# Revit family: 54212209(2024)
name_source: partatom
category: Plumbing Fixtures
units: mm (PartAtom-declared; Revit-internal decimal feet)

## family parameters
Always vertical = Yes
Cut with Voids When Loaded = No
OmniClass Number = 23.45.55.00
OmniClass Title = Sanitary Faucets, Wastes
Part Type = Normal
Room Calculation Point = No
Round Connector Dimension = Use Diameter
Shared = No
Work Plane-Based = No

## types (3) — shared parameters
2D/3D/BIM Files URL = http://static.hansa.com
3D View = https://static.hansa.com
Advanced Features = Inner body made of DZR brass
Aerator = Standard aerator
AssetType = Fixed
Automatic Flush Frequency = 30 s (1-1800 s)
Automatic Flush Period = 30 s (1-1800 s)
Backflow Prevention EN1717 = EB
Bluetooth = 5.x (D060576)
BodyMaterial = Brass
Brand = HANSA
Catalog Drawing URL = http://static.hansa.com
Connection = Flexible inlet pipes
Connection Size = G3/8
Dimension Drawing URL = http://static.hansa.com
DurationUnit = Year
EMC Directive = Radio Equipment Directive 2014/53/EU , 
Low Voltage Directive 2014/35/EU , 
EMC Directive 2014/30/EU , 
RoHS Directive 2011/65/EU
EN Standard = ETSI EN 301 489-1 V1.9.2 , 
ETSI EN 300 328 v2.2.2 , 
EN 61000-6-1:2007 , 
EN 61000-6-3:2007+A1:2011+AC:2012 , 
EN 60335-1:2012+A11+A13+A1+A14+A2+A15:2021, Part 19.11.4
ETIM Class Number = EC011431 Kitchen mixing tap
FDV Document URL = http://www.hansa.com
Finish = Polished
Flow Drawing URL = http://static.hansa.com
Flow Rate At 300kPa With Flow Controller = 0.2 L/s
Group = Kitchen faucet
IfcExportAs = IfcValveType
IfcExportType = FAUCET
InletConnectionSize = 10 mm  [stored 0.0328084 ft]
Installation Type = Deck mounted
Installation and Maintenance Guide URL = http://static.hansa.com
Interactive AR View URL = https://static.hansa.com
Lever Handle = Single operating lever/handle;Hot/Cold symbols
Manufacturer = HANSA
ManufacturerName = HANSA
ManufacturerURL = http://www.hansa.com
Market = International;Germany;Austria;Belgium;Netherlands;Czech Republic;Slovakia;Italy
Material = Brass
Max Flow Period = 10 s (1-1800s)
Max. Hot Water Supply = 70 °C
Mobile Product Information URL = http://mpi.hansa.com
NBSDescription = Water supply fittings for wash basins and troughs
NBSReference = 45-35-70/371
Noise Class = I (ISO 3822)
NominalDepth = 259 mm  [stored 0.849738 ft]
NominalHeight = 330 mm
NominalWidth = 50 mm  [stored 0.164042 ft]
Operating Distance = 0-30 mm ( 30/90/110/130 mm)
Product Family = HANSAVANTIS Style Hybrid
Product Image URL = http://static.hansa.com
Product URL = http://static.hansa.com
ProductInformation = Kitchen faucet with high spout
Sales Package dimensions (LxWxH) = 508 x 249 x 96
Shape = Sculptured
Size = 54x261.5x338 mm
Spout Projection = 255 mm
Spout Swivel Range = 120°
Spout Type = Swivel spout
Technical DataSheet URL = http://www.hansa.com
Temperature Adjustments = Limitation option for maximum temperature and flow-rate
UNSPSC Class Number = 30181700 Faucets or taps
URL Declaration Of Performance (DOP) = http://static.hansa.com
URL Declaration of Asbestos = http://static.hansa.com
URL Declaration of Conformity = http://static.hansa.com
URL Declaration of SCIP = http://static.hansa.com
URL EU Packaging Declaration = http://static.hansa.com
URL EcoLabel Declaration = http://static.hansa.com
URL REACH = http://static.hansa.com
URL UWL = http://static.hansa.com
URL WEEE = http://static.hansa.com
Uniclass2 = Pr_40_30_96_96
Uniclass2015Description = Washbasin manual water supply sets
Uniclass2015Reference = Pr_40_20_87_96
Version = 1
VersionDate = 20/04/2024
Warranty Information URL = http://warranty.hansa.com
WarrantyDescription = http://warranty.hansa.com
WarrantyDurationUnit = Year
Working Pressure = 50 - 1000 kPa
zero-valued in all types: CloseOffRating, Default Elevation, FlowCoefficient

## per-type parameters (varying)
| type | BIMObjectName | Color | EAN Number | Electrical Connection | Electronic Parts | FaucetMainMaterial | Features | Flow Rate At 300kPa | Mechanical Parts | ModelReference | Mounting Holes | Operating Voltage | Product Code | Protection Class | Spare-Part Information URL | Surface treatment | Type | URL Materials Declaration |
| 54212209 Kitchen faucet | 54212209(2024) | Chrome | 4057304019890 |  | Solenoid valve;Power supply | Chrome | Hybrid Hybrid;Plug transformer;Bluetooth® | 0.0 L/s | 30Cartridge | 54212209 |  | 2309 V | 54212209 | IP 55 |  | Chrome | 0 |  |
| 5421220980 Kitchen faucet, 230/9 V, Bluetooth | 5421220980(2024) | Brushed steel | 4057304022142 | 230 / 9 V | ;Solenoid valve;Power supply | Brushed Steel | Hybrid;Plug transformer;Bluetooth® | 0.2 L/s | 30EcoCartridge | 5421220980 | 1 hole | 9 V | 5421220980 | IP 55 / transformer IP 20 | http://static.hansa.com | Brushed steel | 80 | http://www.hansa.com |
| 5421220981 Kitchen faucet, 230/9 V, Bluetooth | 5421220981(2024) | BrushedBronze | 4057304022159 | 230 / 9 V | ;Solenoid valve;Power supply | Brushed Bronze | Hybrid;Plug transformer;Bluetooth® | 0.2 L/s | 30EcoCartridge | 5421220981 | 1 hole | 9 V | 5421220981 | IP 55 / transformer IP 20 | http://static.hansa.com | BrushedBronze | 81 | http://www.hansa.com |

note: column(s) folded — value = type name in every type: Model, Name, Name_en

note: [stored X ft] marks values corroborated as IEEE doubles in the binary element streams (Revit-internal decimal feet)

## geometry (parser evidence)
native form markers: Sweep x5
no freeform markers — native parametric forms only
